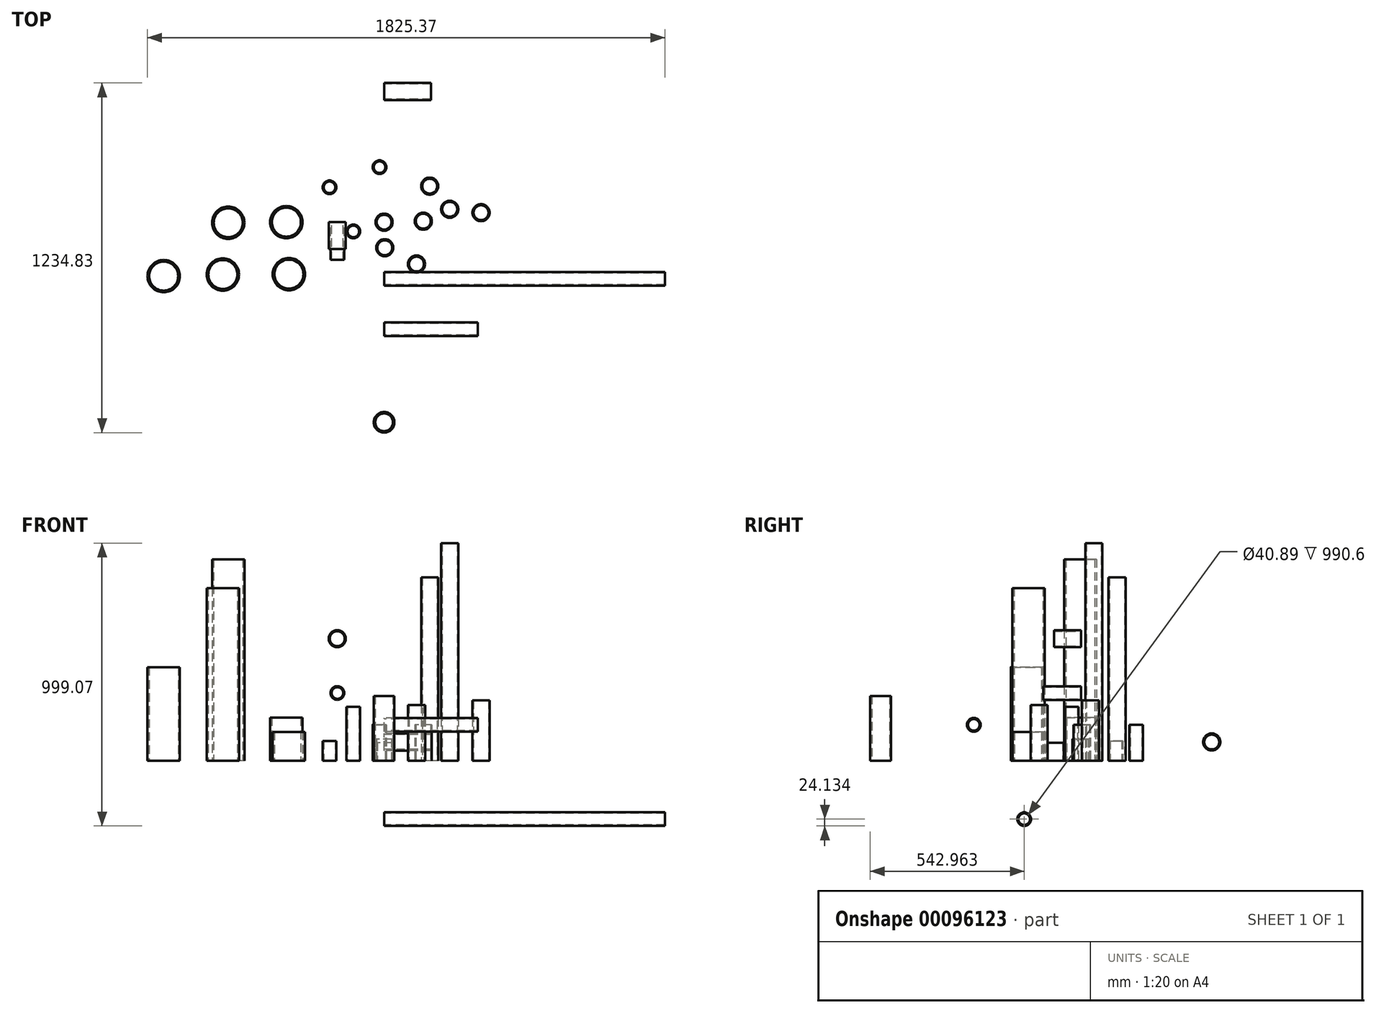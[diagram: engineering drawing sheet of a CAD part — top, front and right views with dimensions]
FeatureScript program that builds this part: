
annotation { "Feature Type Name" : "Feature", "Feature Type Description" : "" }
export const myFeature = defineFeature(function(context is Context, id is Id, definition is map)
    precondition{}
    {
        {
            var Q0;
            Q0=qCreatedBy(makeId("Top.planeOp"),FACE);
            var sketch = newSketch(context, id + "F0", { "sketchPlane" : qUnion([Q0])});
            skCircle(sketch, "E0", {"center": v(0, 0) * mm, "radius": 30.16 * mm});
            skCircle(sketch, "E1", {"center": v(0, 0) * mm, "radius": 26.25 * mm});
            skSolve(sketch);
        }
        {
            var Q0;
            Q0=makeQuery(id+"F0.imprint","IMPRINT",FACE,{"disambiguationData":[TD([[makeQuery(id+"F0.imprint","IMPRINT",EDGE,{"derivedFrom":sQuery(id+"F0.wireOp",EDGE,"E0")}),1.0]])]});
            extrude(context, id + "F1", {"entities" : qUnion([Q0]), "depth" : 76.2 * mm});
        }
        {
            var Q0;
            Q0=qCreatedBy(makeId("Top.planeOp"),FACE);
            var sketch = newSketch(context, id + "F2", { "sketchPlane" : qUnion([Q0])});
            skCircle(sketch, "E2", {"center": v(138.3, 3.34) * mm, "radius": 30.16 * mm});
            skCircle(sketch, "E3", {"center": v(138.3, 3.34) * mm, "radius": 26.25 * mm});
            skSolve(sketch);
        }
        {
            var Q0;
            Q0=makeQuery(id+"F2.imprint","IMPRINT",FACE,{"disambiguationData":[TD([[makeQuery(id+"F2.imprint","IMPRINT",EDGE,{"derivedFrom":sQuery(id+"F2.wireOp",EDGE,"E2")}),1.0]])]});
            extrude(context, id + "F3", {"entities" : qUnion([Q0]), "depth" : 127 * mm});
        }
        {
            var Q0;
            Q0=qCreatedBy(makeId("Top.planeOp"),FACE);
            var sketch = newSketch(context, id + "F4", { "sketchPlane" : qUnion([Q0])});
            skCircle(sketch, "E4", {"center": v(231.52, 45.5) * mm, "radius": 30.16 * mm});
            skCircle(sketch, "E5", {"center": v(231.52, 45.5) * mm, "radius": 26.25 * mm});
            skSolve(sketch);
        }
        {
            var Q0;
            Q0=makeQuery(id+"F4.imprint","IMPRINT",FACE,{"disambiguationData":[TD([[makeQuery(id+"F4.imprint","IMPRINT",EDGE,{"derivedFrom":sQuery(id+"F4.wireOp",EDGE,"E4")}),1.0]])]});
            extrude(context, id + "F5", {"entities" : qUnion([Q0]), "depth" : 768.35 * mm});
        }
        {
            var Q0;
            Q0=qCreatedBy(makeId("Right.planeOp"),FACE);
            var sketch = newSketch(context, id + "F6", { "sketchPlane" : qUnion([Q0])});
            skCircle(sketch, "E6", {"center": v(461.28, 65.95) * mm, "radius": 30.16 * mm});
            skCircle(sketch, "E7", {"center": v(461.28, 65.95) * mm, "radius": 26.25 * mm});
            skSolve(sketch);
        }
        {
            var Q0;
            Q0=makeQuery(id+"F6.imprint","IMPRINT",FACE,{"disambiguationData":[TD([[makeQuery(id+"F6.imprint","IMPRINT",EDGE,{"derivedFrom":sQuery(id+"F6.wireOp",EDGE,"E6")}),1.0]])]});
            extrude(context, id + "F7", {"entities" : qUnion([Q0]), "depth" : 165.1 * mm});
        }
        {
            var Q0;
            Q0=qCreatedBy(makeId("Top.planeOp"),FACE);
            var sketch = newSketch(context, id + "F8", { "sketchPlane" : qUnion([Q0])});
            skCircle(sketch, "E8", {"center": v(-192.6, 123.01) * mm, "radius": 24.13 * mm});
            skCircle(sketch, "E9", {"center": v(-192.6, 123.01) * mm, "radius": 20.45 * mm});
            skSolve(sketch);
        }
        {
            var Q0;
            Q0=qCreatedBy(makeId("Front.planeOp"),FACE);
            var sketch = newSketch(context, id + "F9", { "sketchPlane" : qUnion([Q0])});
            skCircle(sketch, "E10", {"center": v(-164.87, 238.92) * mm, "radius": 24.13 * mm});
            skCircle(sketch, "E11", {"center": v(-164.87, 238.92) * mm, "radius": 20.45 * mm});
            skSolve(sketch);
        }
        {
            var Q0;
            Q0=qSketchRegion(id+"F9",true);
            extrude(context, id + "F10", {"entities" : qUnion([Q0]), "depth" : 133.35 * mm});
        }
        {
            var Q0;
            Q0=qCreatedBy(makeId("Right.planeOp"),FACE);
            var sketch = newSketch(context, id + "F11", { "sketchPlane" : qUnion([Q0])});
            skCircle(sketch, "E12", {"center": v(-378.27, 126.43) * mm, "radius": 20.45 * mm});
            skCircle(sketch, "E13", {"center": v(-378.27, 126.43) * mm, "radius": 24.13 * mm});
            skSolve(sketch);
        }
        {
            var Q0;
            Q0=qSketchRegion(id+"F11",true);
            extrude(context, id + "F12", {"entities" : qUnion([Q0]), "depth" : 330.2 * mm});
        }
        {
            var Q0;
            Q0=qCreatedBy(makeId("Top.planeOp"),FACE);
            var sketch = newSketch(context, id + "F13", { "sketchPlane" : qUnion([Q0])});
            skCircle(sketch, "E14", {"center": v(-16.24, 194.12) * mm, "radius": 24.13 * mm});
            skCircle(sketch, "E15", {"center": v(-16.24, 194.12) * mm, "radius": 20.45 * mm});
            skSolve(sketch);
        }
        {
            var Q0;
            Q0=qSketchRegion(id+"F13",true);
            extrude(context, id + "F14", {"entities" : qUnion([Q0]), "depth" : 127 * mm});
        }
        {
            var Q0;
            Q0=qCreatedBy(makeId("Right.planeOp"),FACE);
            var sketch = newSketch(context, id + "F15", { "sketchPlane" : qUnion([Q0])});
            skCircle(sketch, "E16", {"center": v(-200.43, -206.59) * mm, "radius": 24.13 * mm});
            skCircle(sketch, "E17", {"center": v(-200.43, -206.59) * mm, "radius": 20.45 * mm});
            skSolve(sketch);
        }
        {
            var Q0;
            Q0=qSketchRegion(id+"F15",true);
            extrude(context, id + "F16", {"entities" : qUnion([Q0]), "depth" : 990.6 * mm});
        }
        {
            var Q0;
            Q0=makeQuery(id+"F8.imprint","IMPRINT",FACE,{"disambiguationData":[TD([[makeQuery(id+"F8.imprint","IMPRINT",EDGE,{"derivedFrom":sQuery(id+"F8.wireOp",EDGE,"E8")}),1.0]])]});
            extrude(context, id + "F17", {"entities" : qUnion([Q0]), "depth" : 69.85 * mm});
        }
        {
            var Q0;
            Q0=qCreatedBy(makeId("Top.planeOp"),FACE);
            var sketch = newSketch(context, id + "F18", { "sketchPlane" : qUnion([Q0])});
            skCircle(sketch, "E18", {"center": v(-108.42, -32.85) * mm, "radius": 24.13 * mm});
            skCircle(sketch, "E19", {"center": v(-108.42, -32.85) * mm, "radius": 20.45 * mm});
            skSolve(sketch);
        }
        {
            var Q0;
            Q0=makeQuery(id+"F18.imprint","IMPRINT",FACE,{"disambiguationData":[TD([[makeQuery(id+"F18.imprint","IMPRINT",EDGE,{"derivedFrom":sQuery(id+"F18.wireOp",EDGE,"E18")}),1.0]])]});
            extrude(context, id + "F19", {"entities" : qUnion([Q0]), "depth" : 190.5 * mm});
        }
        {
            var Q0;
            Q0=qCreatedBy(makeId("Top.planeOp"),FACE);
            var sketch = newSketch(context, id + "F20", { "sketchPlane" : qUnion([Q0])});
            skCircle(sketch, "E20", {"center": v(160.85, 127.18) * mm, "radius": 30.16 * mm});
            skCircle(sketch, "E21", {"center": v(160.85, 127.18) * mm, "radius": 26.25 * mm});
            skSolve(sketch);
        }
        {
            var Q0;
            Q0=makeQuery(id+"F20.imprint","IMPRINT",FACE,{"disambiguationData":[TD([[makeQuery(id+"F20.imprint","IMPRINT",EDGE,{"derivedFrom":sQuery(id+"F20.wireOp",EDGE,"E20")}),1.0]])]});
            extrude(context, id + "F21", {"entities" : qUnion([Q0]), "depth" : 647.7 * mm});
        }
        {
            var Q0;
            Q0=qCreatedBy(makeId("Top.planeOp"),FACE);
            var sketch = newSketch(context, id + "F22", { "sketchPlane" : qUnion([Q0])});
            skCircle(sketch, "E22", {"center": v(-345, 0) * mm, "radius": 57.15 * mm});
            skCircle(sketch, "E23", {"center": v(-345, 0) * mm, "radius": 51.13 * mm});
            skSolve(sketch);
        }
        {
            var Q0;
            Q0=makeQuery(id+"F22.imprint","IMPRINT",FACE,{"disambiguationData":[TD([[makeQuery(id+"F22.imprint","IMPRINT",EDGE,{"derivedFrom":sQuery(id+"F22.wireOp",EDGE,"E22")}),1.0]])]});
            extrude(context, id + "F23", {"entities" : qUnion([Q0]), "depth" : 152.4 * mm});
        }
        {
            var Q0;
            Q0=qCreatedBy(makeId("Top.planeOp"),FACE);
            var sketch = newSketch(context, id + "F24", { "sketchPlane" : qUnion([Q0])});
            skCircle(sketch, "E24", {"center": v(-549.98, -2.17) * mm, "radius": 57.15 * mm});
            skCircle(sketch, "E25", {"center": v(-549.98, -2.17) * mm, "radius": 51.13 * mm});
            skSolve(sketch);
        }
        {
            var Q0;
            Q0=makeQuery(id+"F24.imprint","IMPRINT",FACE,{"disambiguationData":[TD([[makeQuery(id+"F24.imprint","IMPRINT",EDGE,{"derivedFrom":sQuery(id+"F24.wireOp",EDGE,"E24")}),1.0]])]});
            extrude(context, id + "F25", {"entities" : qUnion([Q0]), "depth" : 711.2 * mm});
        }
        {
            var Q0;
            Q0=qCreatedBy(makeId("Top.planeOp"),FACE);
            var sketch = newSketch(context, id + "F26", { "sketchPlane" : qUnion([Q0])});
            skCircle(sketch, "E26", {"center": v(-335.9, -183.7) * mm, "radius": 57.15 * mm});
            skCircle(sketch, "E27", {"center": v(-335.9, -183.7) * mm, "radius": 51.13 * mm});
            skSolve(sketch);
        }
        {
            var Q0;
            Q0=makeQuery(id+"F26.imprint","IMPRINT",FACE,{"disambiguationData":[TD([[makeQuery(id+"F26.imprint","IMPRINT",EDGE,{"derivedFrom":sQuery(id+"F26.wireOp",EDGE,"E26")}),1.0]])]});
            extrude(context, id + "F27", {"entities" : qUnion([Q0]), "depth" : 101.6 * mm});
        }
        {
            var Q0;
            Q0=qCreatedBy(makeId("Top.planeOp"),FACE);
            var sketch = newSketch(context, id + "F28", { "sketchPlane" : qUnion([Q0])});
            skCircle(sketch, "E28", {"center": v(-568.97, -184.87) * mm, "radius": 57.15 * mm});
            skCircle(sketch, "E29", {"center": v(-568.97, -184.87) * mm, "radius": 51.13 * mm});
            skSolve(sketch);
        }
        {
            var Q0;
            Q0=makeQuery(id+"F28.imprint","IMPRINT",FACE,{"disambiguationData":[TD([[makeQuery(id+"F28.imprint","IMPRINT",EDGE,{"derivedFrom":sQuery(id+"F28.wireOp",EDGE,"E28")}),1.0]])]});
            extrude(context, id + "F29", {"entities" : qUnion([Q0]), "depth" : 609.6 * mm});
        }
        {
            var Q0;
            Q0=qCreatedBy(makeId("Top.planeOp"),FACE);
            var sketch = newSketch(context, id + "F30", { "sketchPlane" : qUnion([Q0])});
            skCircle(sketch, "E30", {"center": v(-777.62, -190.68) * mm, "radius": 57.15 * mm});
            skCircle(sketch, "E31", {"center": v(-777.62, -190.68) * mm, "radius": 51.13 * mm});
            skSolve(sketch);
        }
        {
            var Q0;
            Q0=makeQuery(id+"F30.imprint","IMPRINT",FACE,{"disambiguationData":[TD([[makeQuery(id+"F30.imprint","IMPRINT",EDGE,{"derivedFrom":sQuery(id+"F30.wireOp",EDGE,"E30")}),1.0]])]});
            extrude(context, id + "F31", {"entities" : qUnion([Q0]), "depth" : 330.2 * mm});
        }
        {
            var Q0;
            Q0=qCreatedBy(makeId("Top.planeOp"),FACE);
            var sketch = newSketch(context, id + "F32", { "sketchPlane" : qUnion([Q0])});
            skCircle(sketch, "E32", {"center": v(342.1, 33.53) * mm, "radius": 30.16 * mm});
            skCircle(sketch, "E33", {"center": v(342.1, 33.53) * mm, "radius": 26.25 * mm});
            skSolve(sketch);
        }
        {
            var Q0;
            Q0=makeQuery(id+"F32.imprint","IMPRINT",FACE,{"disambiguationData":[TD([[makeQuery(id+"F32.imprint","IMPRINT",EDGE,{"derivedFrom":sQuery(id+"F32.wireOp",EDGE,"E32")}),1.0]])]});
            extrude(context, id + "F33", {"entities" : qUnion([Q0]), "depth" : 212.72 * mm});
        }
        {
            var Q0;
            Q0=qCreatedBy(makeId("Front.planeOp"),FACE);
            var sketch = newSketch(context, id + "F34", { "sketchPlane" : qUnion([Q0])});
            skCircle(sketch, "E34", {"center": v(-165.35, 430.8) * mm, "radius": 30.16 * mm});
            skCircle(sketch, "E35", {"center": v(-165.35, 430.8) * mm, "radius": 26.25 * mm});
            skSolve(sketch);
        }
        {
            var Q0;
            Q0=makeQuery(id+"F34.imprint","IMPRINT",FACE,{"disambiguationData":[TD([[makeQuery(id+"F34.imprint","IMPRINT",EDGE,{"derivedFrom":sQuery(id+"F34.wireOp",EDGE,"E34")}),1.0]])]});
            extrude(context, id + "F35", {"entities" : qUnion([Q0]), "depth" : 95.25 * mm});
        }
        {
            var Q0;
            Q0=qCreatedBy(makeId("Top.planeOp"),FACE);
            var sketch = newSketch(context, id + "F36", { "sketchPlane" : qUnion([Q0])});
            skCircle(sketch, "E36", {"center": v(2.35, -90.32) * mm, "radius": 30.16 * mm});
            skCircle(sketch, "E37", {"center": v(2.35, -90.32) * mm, "radius": 26.25 * mm});
            skSolve(sketch);
        }
        {
            var Q0;
            Q0=makeQuery(id+"F36.imprint","IMPRINT",FACE,{"disambiguationData":[TD([[makeQuery(id+"F36.imprint","IMPRINT",EDGE,{"derivedFrom":sQuery(id+"F36.wireOp",EDGE,"E36")}),1.0]])]});
            extrude(context, id + "F37", {"entities" : qUnion([Q0]), "depth" : 63.5 * mm});
        }
        {
            var Q0;
            Q0=qCreatedBy(makeId("Top.planeOp"),FACE);
            var sketch = newSketch(context, id + "F38", { "sketchPlane" : qUnion([Q0])});
            skCircle(sketch, "E38", {"center": v(114.34, -147.96) * mm, "radius": 30.16 * mm});
            skCircle(sketch, "E39", {"center": v(114.34, -147.96) * mm, "radius": 26.25 * mm});
            skSolve(sketch);
        }
        {
            var Q0;
            Q0=makeQuery(id+"F38.imprint","IMPRINT",FACE,{"disambiguationData":[TD([[makeQuery(id+"F38.imprint","IMPRINT",EDGE,{"derivedFrom":sQuery(id+"F38.wireOp",EDGE,"E38")}),1.0]])]});
            extrude(context, id + "F39", {"entities" : qUnion([Q0]), "depth" : 196.85 * mm});
        }
        {
            var Q0;
            Q0=qCreatedBy(makeId("Top.planeOp"),FACE);
            var sketch = newSketch(context, id + "F40", { "sketchPlane" : qUnion([Q0])});
            skCircle(sketch, "E40", {"center": v(0, -706.88) * mm, "radius": 31.36 * mm});
            skCircle(sketch, "E41", {"center": v(0, -706.88) * mm, "radius": 36.51 * mm});
            skSolve(sketch);
        }
        {
            var Q0;
            Q0=makeQuery(id+"F40.imprint","IMPRINT",FACE,{"disambiguationData":[TD([[makeQuery(id+"F40.imprint","IMPRINT",EDGE,{"derivedFrom":sQuery(id+"F40.wireOp",EDGE,"E40")}),-1.0]])]});
            extrude(context, id + "F41", {"entities" : qUnion([Q0]), "depth" : 228.6 * mm});
        }
    });
